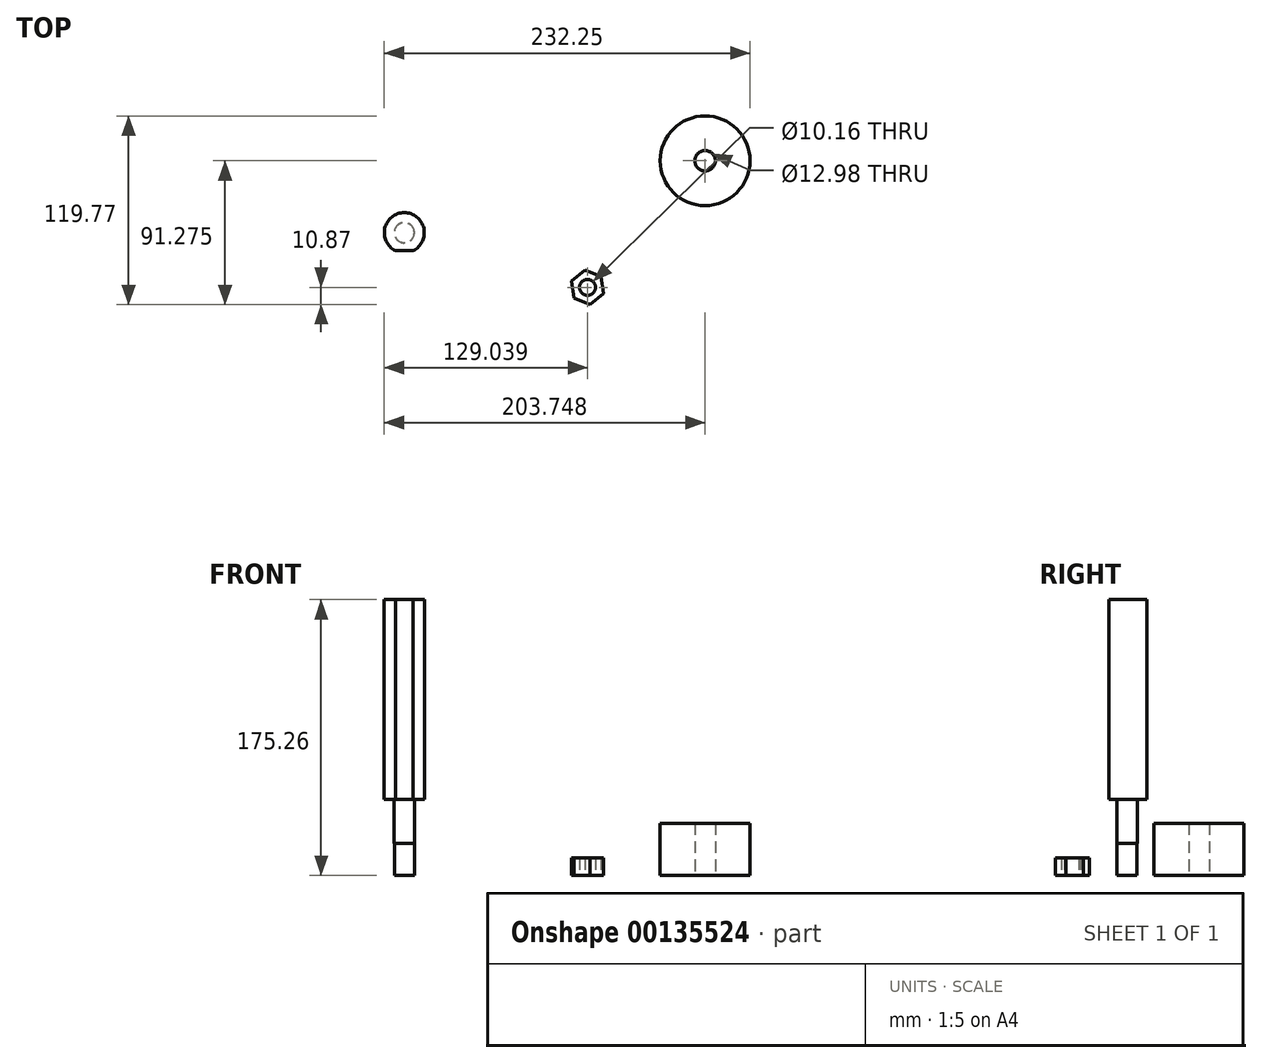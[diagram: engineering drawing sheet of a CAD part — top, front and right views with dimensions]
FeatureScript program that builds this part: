
annotation { "Feature Type Name" : "Feature", "Feature Type Description" : "" }
export const myFeature = defineFeature(function(context is Context, id is Id, definition is map)
    precondition{}
    {
        {
            var Q0;
            Q0=qCreatedBy(makeId("Right.planeOp"),FACE);
            var sketch = newSketch(context, id + "F0", { "sketchPlane" : qUnion([Q0])});
            skLineSegment(sketch, "E0", {"start": v(12.7, 175.26) * mm, "end": v(12.7, 48.26) * mm});
            skLineSegment(sketch, "E1", {"start": v(12.7, 48.26) * mm, "end": v(6.48, 48.26) * mm});
            skLineSegment(sketch, "E2", {"start": v(6.48, 48.26) * mm, "end": v(6.48, 20.32) * mm});
            skLineSegment(sketch, "E3", {"start": v(6.48, 20.32) * mm, "end": v(6.35, 20.32) * mm});
            skLineSegment(sketch, "E4", {"start": v(6.35, 20.32) * mm, "end": v(6.35, 0) * mm});
            skLineSegment(sketch, "E5", {"start": v(6.35, 0) * mm, "end": v(0, 0) * mm});
            skLineSegment(sketch, "E6", {"start": v(0, 0) * mm, "end": v(0, 175.26) * mm});
            skLineSegment(sketch, "E7", {"start": v(0, 175.26) * mm, "end": v(12.7, 175.26) * mm});
            skSolve(sketch);
        }
        {
            var Q0;
            Q0 = qSketchRegion(id + "F0", true);
            var Q1;
            Q1=sQuery(id+"F0.wireOp",EDGE,"E6");
            revolve(context, id + "F1", {"entities" : qUnion([Q0]), "axis" : qUnion([Q1]), "revolveType" : RevolveType.FULL});
        }
        {
            var Q0;
            Q0=makeQuery(id+"F1.opRevolve","SWEPT_FACE",FACE,{"disambiguationData":[OSD([sQuery(id+"F0.wireOp",EDGE,"E1")])]});
            var sketch = newSketch(context, id + "F2", { "sketchPlane" : qUnion([Q0])});
            skLineSegment(sketch, "E8.bottom", {"start": v(-5.54, 13.97) * mm, "end": v(5.54, 13.97) * mm});
            skLineSegment(sketch, "E8.top", {"start": v(-5.54, 11.43) * mm, "end": v(5.54, 11.43) * mm});
            skLineSegment(sketch, "E8.left", {"start": v(-5.54, 13.97) * mm, "end": v(-5.54, 11.43) * mm});
            skLineSegment(sketch, "E8.right", {"start": v(5.54, 13.97) * mm, "end": v(5.54, 11.43) * mm});
            skSolve(sketch);
        }
        {
            var Q0;
            Q0 = qSketchRegion(id + "F2", true);
            extrude(context, id + "F3", {"entities" : qUnion([Q0]), "operationType" : NewBodyOperationType.REMOVE, "endBound" : BoundingType.THROUGH_ALL, "oppositeDirection" : true, "depth" : 25.4 * mm});
        }
        {
            var Q0;
            Q0=qCreatedBy(makeId("Top.planeOp"),FACE);
            var sketch = newSketch(context, id + "F4", { "sketchPlane" : qUnion([Q0])});
            skCircle(sketch, "E9", {"center": v(191.05, 45.66) * mm, "radius": 28.5 * mm});
            skCircle(sketch, "E10", {"center": v(191.05, 45.66) * mm, "radius": 6.49 * mm});
            skSolve(sketch);
        }
        {
            var Q0;
            Q0 = qSketchRegion(id + "F4", true);
            extrude(context, id + "F5", {"entities" : qUnion([Q0]), "depth" : 33.27 * mm});
        }
        {
            var Q0;
            Q0=qCreatedBy(makeId("Top.planeOp"),FACE);
            var sketch = newSketch(context, id + "F6", { "sketchPlane" : qUnion([Q0])});
            skCircle(sketch, "E11.cCircle", {"center": v(116.34, -34.74) * mm, "radius": 9.53 * mm, "construction": true});
            skLineSegment(sketch, "E11.0", {"start": v(126.58, -38.74) * mm, "end": v(118, -45.61) * mm});
            skLineSegment(sketch, "E11.1", {"start": v(118, -45.61) * mm, "end": v(107.75, -41.61) * mm});
            skLineSegment(sketch, "E11.2", {"start": v(107.75, -41.61) * mm, "end": v(106.1, -30.74) * mm});
            skLineSegment(sketch, "E11.3", {"start": v(106.1, -30.74) * mm, "end": v(114.68, -23.87) * mm});
            skLineSegment(sketch, "E11.4", {"start": v(114.68, -23.87) * mm, "end": v(124.93, -27.87) * mm});
            skLineSegment(sketch, "E11.5", {"start": v(124.93, -27.87) * mm, "end": v(126.58, -38.74) * mm});
            skPoint(sketch, "E11.0.midPoint", {"position": v(122.29, -42.18) * mm});
            skCircle(sketch, "E12", {"center": v(116.34, -34.74) * mm, "radius": 5.08 * mm});
            skSolve(sketch);
        }
        {
            var Q0;
            Q0 = qSketchRegion(id + "F6", true);
            extrude(context, id + "F7", {"entities" : qUnion([Q0]), "depth" : 11.1 * mm});
        }
    });
